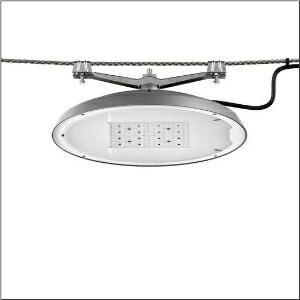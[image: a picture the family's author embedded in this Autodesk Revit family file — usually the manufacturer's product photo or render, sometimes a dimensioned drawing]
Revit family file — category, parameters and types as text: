
# Revit family: dl_50_iq_mini___st0_8s_5xa248v41f08me_f8fe
name_source: partatom
category: Lighting Fixtures
units: mm (PartAtom-declared; Revit-internal decimal feet)

## family parameters
Cut with Voids When Loaded = No
Host = Face
Light Source = No
Part Type = Normal
Room Calculation Point = No
Round Connector Dimension = Use Diameter
Shared = No

## types (1)
- --- (1 x LED, 15660 lm, 101.7 W, 4000K)
    Apparent Load = 102 VA
    CIE Flux Codes = 38 75 97 100 100
    Color Rendering = 70
    Color Temperature = 4000K
    Default Elevation = 1800 mm
    Description = DL 50 iQ mini, catenary luminaire, primary light control with lens, of PMMA, primary optical cover: cover, of toughened safety glass, transparent, light distribution: ST0.8s, light emission: direct distribution, primary light characteristic: symmetric, installation type: suspended mounting, LED, High Power LED, rated luminous flux: 15.660lm, luminous efficacy: 154lm/W, light colour: 740, colour temperature: 4000K, control gear: iQ Street-Remote, control: optimised constant luminous flux control (CLO 2.0), Desk-Remote (wireless, voltage-free reading and setting of iQ features in the workshop via application-optimized NFC function/RFID function), Light-Fading, Smart-Wire, Night-Set, Lumen-Switch, Temp-Guard, Auto-Match, Street-Remote, mains connection: 230..240V, AC, 50/60Hz, start of lifetime: 102W, end of service life: 111W, reduction: 45W, luminaire housing, of diecast aluminium, powder-coated, SITECO metallic grey (DB 702S), diameter: 500mm, height: 115mm, mounting height: 4..12m, protection rating (complete): IP66, insulation class (complete): insulation class II (safety insulation), certification: CE, ENEC, ENEC+, VDE, impact resistance: IK08, permissible operating ambient temperature for outdoor applications: -25..+40°C, standard-compliant lighting for roads and squares, packaging unit: 1 piece

Light Distribution: ST0.8s
    Height = 124 mm  [stored 0.406824 ft]
    Lamp = 1 x LED
    Lamp Light Flux = 15660 lm
    Lamp Power = 101.7 W
    Lamp count = 1
    Length = 500 mm
    Luminous efficacy = 154 lm/W
    Manufacturer = Siteco
    ModVariant = No
    Model = 5XA248V41F08ME
    Number of Poles = 1
    OnlyDefault = Yes
    Power Factor = 1
    Product Name = DL 50 iQ mini | ST0.8s
    Product group = catenary luminaire
    ProductGroupID = 6300
    Protection Class = Protection class II
    Protection Degree = IP 66
    RLX_Detail_Level = 1
    RLX_Emergency_Light_Flux = 0 lm
    RLX_Emergency_Type = 0
    RLX_Emergency_Type_DB = No
    RlxData = <blob elided: 126957 chars, md5=61dffd52>
    Socket = socket
    Standby Power = 0 W
    System Light Flux = 15660 lm
    System Power = 102 W
    Type Comments = factory setting: luminous flux: 100 % | dim-lin: 254 | 534 mA
    Type Image = l_1251783.jpg
    URL = http://relux.com
    VarID = @adj_140439
    Voltage = 0 V
    Weight = 0.00 kg
    Width = 0 mm  [stored 0 ft]

note: [stored X ft] marks values corroborated as IEEE doubles in the binary element streams (Revit-internal decimal feet)

## geometry (parser evidence)
native form markers: Blend x4, Sweep x13
no freeform markers — native parametric forms only
